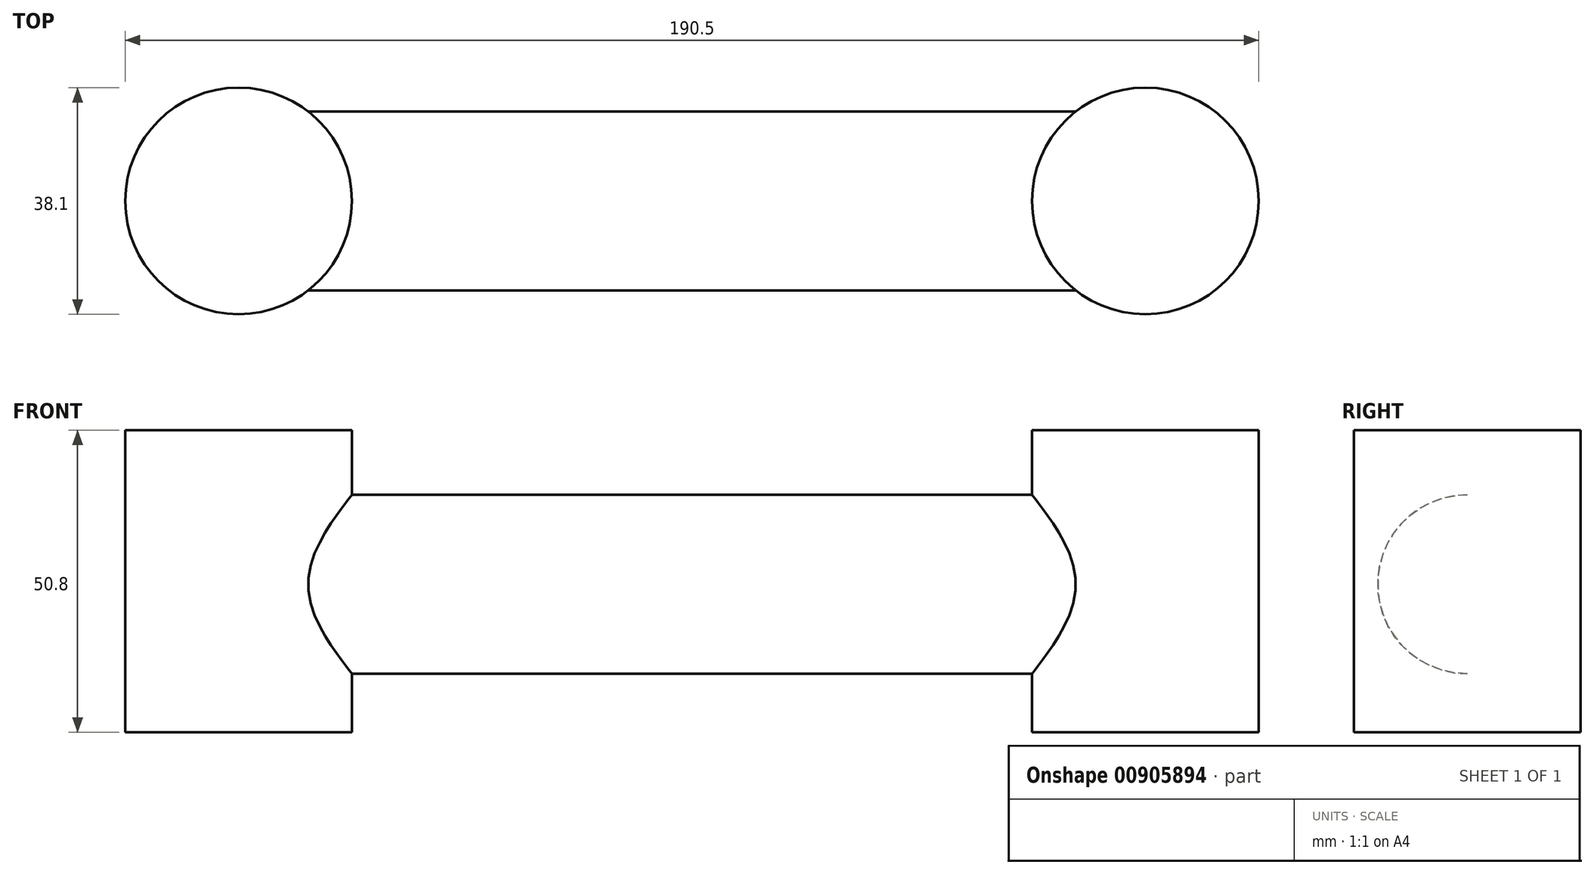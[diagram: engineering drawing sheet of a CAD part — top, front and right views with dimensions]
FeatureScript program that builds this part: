
annotation { "Feature Type Name" : "Feature", "Feature Type Description" : "" }
export const myFeature = defineFeature(function(context is Context, id is Id, definition is map)
    precondition{}
    {
        {
            var Q0;
            Q0=qCreatedBy(makeId("Top.planeOp"),FACE);
            var sketch = newSketch(context, id + "F0", { "sketchPlane" : qUnion([Q0])});
            skCircle(sketch, "E0", {"center": v(0, 0) * mm, "radius": 19.05 * mm});
            skCircle(sketch, "E1.1.0.0", {"center": v(-152.4, 0) * mm, "radius": 19.05 * mm});
            skLineSegment(sketch, "E1.direction1", {"start": v(0, 0) * mm, "end": v(-152.4, 0) * mm, "construction": true});
            skSolve(sketch);
        }
        {
            var Q0;
            Q0 = qSketchRegion(id + "F0", true);
            var Q1;
            Q1=sQuery(id+"F0.wireOp",EDGE,"E0");
            var Q2;
            Q2=sQuery(id+"F0.wireOp",EDGE,"E1.1.0.0");
            extrude(context, id + "F1", {"entities" : qUnion([Q0]), "surfaceEntities" : qUnion([Q1, Q2]), "depth" : 50.8 * mm, "offsetDistance" : 25.4 * mm});
        }
        {
            var Q0;
            Q0=qCreatedBy(makeId("Right.planeOp"),FACE);
            var sketch = newSketch(context, id + "F2", { "sketchPlane" : qUnion([Q0])});
            skCircle(sketch, "E2", {"center": v(0, 24.9) * mm, "radius": 15.05 * mm});
            skSolve(sketch);
        }
        {
            var Q0;
            Q0 = qSketchRegion(id + "F2", true);
            extrude(context, id + "F3", {"entities" : qUnion([Q0]), "operationType" : NewBodyOperationType.ADD, "surfaceOperationType" : NewSurfaceOperationType.ADD, "oppositeDirection" : true, "depth" : 152.4 * mm, "offsetDistance" : 25.4 * mm});
        }
    });
